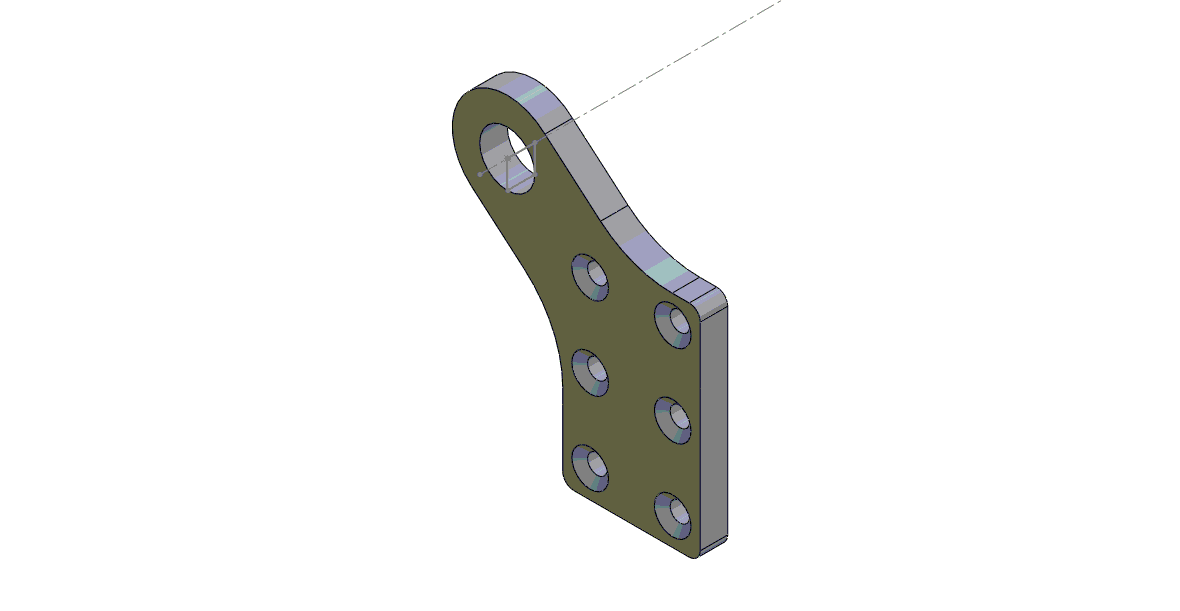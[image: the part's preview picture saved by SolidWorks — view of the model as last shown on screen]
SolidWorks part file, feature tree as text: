
SOLIDWORKS PART (.sldprt)
format: sldprt  version: not decoded by parser v0  size: 218,112 bytes
history: native  units: mm
features: sketch x5, hole x2, material x1, extrude x1 (+13 scaffold rows collapsed)
feature tree (22):
  scaffold x13  (default folders/planes/origin — collapsed)
  material  "Material <not specified>"
  sketch  "Sketch1"  dims[c1.D2=25.4mm c1.D4=25.4mm c1.D5=25.4mm c1.D7=25.4mm c1.D9=25.4mm c2.D2=~33.611058mm c2.D3=~276.034246mm c2.D5=~11.925047mm c2.D6=~19.291652mm c2.D8=~19.829248mm c2.D9=~28.430752mm c2.D10=~4.570261mm c2.D1=0.0mm]
  extrude  "Boss-Extrude1"  Depth=6.35mm
  hole  "CSK for #8 Flat Head Machine Screw (100)1"  Diameter=4.4958mm Depth=6.35mm
  sketch  "Sketch2"
  sketch  "Sketch3"  dims[Thru Hole Dia.=4.4958mm Thru Hole Depth=6.35mm Near C'Sink Dia.=8.4328mm Near C'Sink Angle=100.0deg]
  hole  "1/2 (0.5) Diameter Hole1"  Diameter=12.7mm Depth=6.35mm
  sketch  "Sketch5"
  sketch  "Sketch4"  dims[hole-wizard template sketch: 60 standard entries collapsed; hole parameters kept: c18.Thru Hole Depth=6.35mm]
decode coverage: 6 of 8 modeling features carry decoded parameters
note: ~ marks probable driven/reference dimensions
note: suppression state not decoded; provenance and decode notes live in map.json
